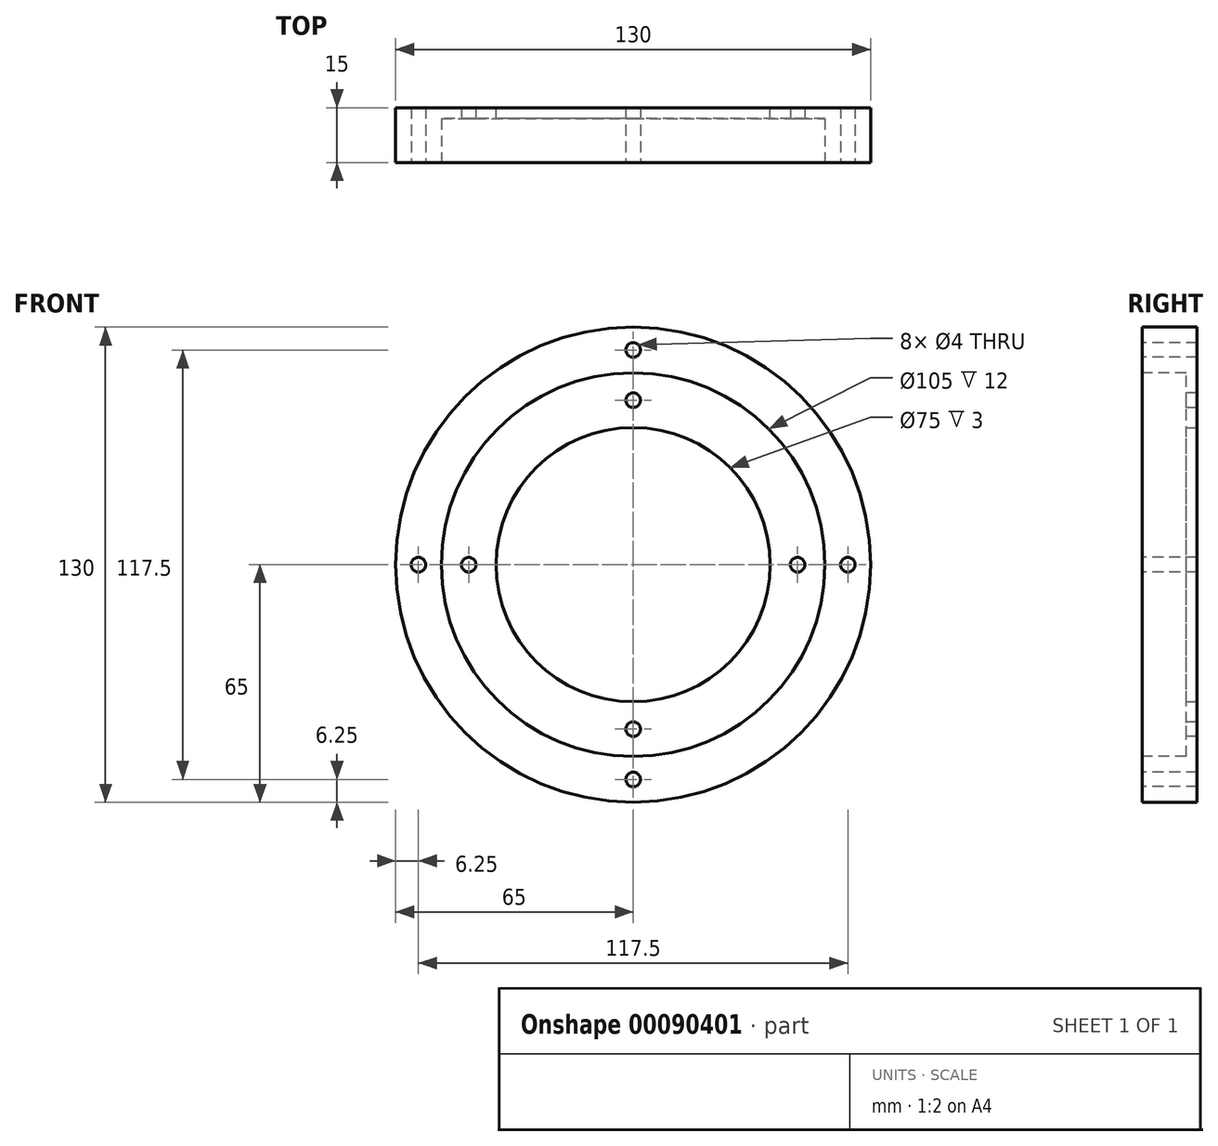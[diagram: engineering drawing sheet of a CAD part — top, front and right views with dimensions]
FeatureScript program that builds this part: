
annotation { "Feature Type Name" : "Feature", "Feature Type Description" : "" }
export const myFeature = defineFeature(function(context is Context, id is Id, definition is map)
    precondition{}
    {
        {
            var Q0;
            Q0=qCreatedBy(makeId("Front.planeOp"),FACE);
            var sketch = newSketch(context, id + "F0", { "sketchPlane" : qUnion([Q0])});
            skCircle(sketch, "E0", {"center": v(0, 0) * mm, "radius": 65 * mm});
            skSolve(sketch);
        }
        {
            var Q0;
            Q0 = qSketchRegion(id + "F0", true);
            extrude(context, id + "F1", {"entities" : qUnion([Q0]), "depth" : 15 * mm});
        }
        {
            var Q0;
            Q0=makeQuery(id+"F1.opExtrude","CAP_FACE",FACE,{"disambiguationData":[OSD([sQuery(id+"F0.wireOp",EDGE,"E0")])],"isStart":false});
            var sketch = newSketch(context, id + "F2", { "sketchPlane" : qUnion([Q0])});
            skCircle(sketch, "E1", {"center": v(0, 0) * mm, "radius": 52.5 * mm});
            skSolve(sketch);
        }
        {
            var Q0;
            Q0=makeQuery(id+"F2.imprint","IMPRINT",FACE,{"disambiguationData":[TD([[makeQuery(id+"F2.imprint","IMPRINT",EDGE,{"derivedFrom":sQuery(id+"F2.wireOp",EDGE,"E1")}),1.0]])]});
            extrude(context, id + "F3", {"entities" : qUnion([Q0]), "operationType" : NewBodyOperationType.REMOVE, "oppositeDirection" : true, "depth" : 12 * mm});
        }
        {
            var Q0;
            Q0=makeQuery(id+"F1.opExtrude","CAP_FACE",FACE,{"disambiguationData":[OSD([sQuery(id+"F0.wireOp",EDGE,"E0")])],"isStart":false});
            var sketch = newSketch(context, id + "F4", { "sketchPlane" : qUnion([Q0])});
            skCircle(sketch, "E2", {"center": v(0, 0) * mm, "radius": 58.75 * mm});
            skPoint(sketch, "E3", {"position": v(0, 58.75) * mm});
            skPoint(sketch, "E4", {"position": v(58.75, 0) * mm});
            skPoint(sketch, "E5", {"position": v(0, -58.75) * mm});
            skPoint(sketch, "E6", {"position": v(-58.75, 0) * mm});
            skSolve(sketch);
        }
        {
            var Q0;
            Q0=sQuery(id+"F4.wireOp",VERTEX,"E6");
            var Q1;
            Q1=sQuery(id+"F4.wireOp",VERTEX,"E3");
            var Q2;
            Q2=sQuery(id+"F4.wireOp",VERTEX,"E4");
            var Q3;
            Q3=sQuery(id+"F4.wireOp",VERTEX,"E5");
            var Q4;
            Q4=makeQuery(id+"F1.opExtrude","SWEPT_BODY",BODY,{"disambiguationData":[OSD([sQuery(id+"F0.wireOp",EDGE,"E0")])]});
            hole(context, id + "F5", {"style" : HoleStyle.SIMPLE, "endStyle" : HoleEndStyle.BLIND, "holeDiameter" : 4 * mm, "holeDepth" : 25 * mm, "startFromSketch" : true, "locations" : qUnion([Q0, Q1, Q2, Q3]), "scope" : qUnion([Q4])});
        }
        {
            var Q0;
            Q0=makeQuery(id+"F3.boolean.opBoolean","COPY",FACE,{"derivedFrom":makeQuery(id+"F3.opExtrude","CAP_FACE",FACE,{"disambiguationData":[OSD([sQuery(id+"F2.wireOp",EDGE,"E1")])],"isStart":false})});
            var sketch = newSketch(context, id + "F6", { "sketchPlane" : qUnion([Q0])});
            skCircle(sketch, "E7", {"center": v(0, 0) * mm, "radius": 45 * mm});
            skPoint(sketch, "E8", {"position": v(-45, 0) * mm});
            skPoint(sketch, "E9", {"position": v(0, -45) * mm});
            skPoint(sketch, "E10", {"position": v(0, 45) * mm});
            skPoint(sketch, "E11", {"position": v(45, 0) * mm});
            skSolve(sketch);
        }
        {
            var Q0;
            Q0=sQuery(id+"F6.wireOp",VERTEX,"E10");
            var Q1;
            Q1=sQuery(id+"F6.wireOp",VERTEX,"E8");
            var Q2;
            Q2=sQuery(id+"F6.wireOp",VERTEX,"E11");
            var Q3;
            Q3=sQuery(id+"F6.wireOp",VERTEX,"E9");
            var Q4;
            Q4=makeQuery(id+"F1.opExtrude","SWEPT_BODY",BODY,{"disambiguationData":[OSD([sQuery(id+"F0.wireOp",EDGE,"E0")])]});
            hole(context, id + "F7", {"style" : HoleStyle.SIMPLE, "endStyle" : HoleEndStyle.BLIND, "holeDiameter" : 4 * mm, "holeDepth" : 25 * mm, "startFromSketch" : true, "locations" : qUnion([Q0, Q1, Q2, Q3]), "scope" : qUnion([Q4])});
        }
        {
            var Q0;
            Q0=makeQuery(id+"F1.opExtrude","CAP_FACE",FACE,{"disambiguationData":[OSD([sQuery(id+"F0.wireOp",EDGE,"E0")])],"isStart":true});
            var sketch = newSketch(context, id + "F8", { "sketchPlane" : qUnion([Q0])});
            skCircle(sketch, "E12", {"center": v(0, 0) * mm, "radius": 37.5 * mm});
            skSolve(sketch);
        }
        {
            var Q0;
            Q0=makeQuery(id+"F8.imprint","IMPRINT",FACE,{"disambiguationData":[TD([[makeQuery(id+"F8.imprint","IMPRINT",EDGE,{"derivedFrom":sQuery(id+"F8.wireOp",EDGE,"E12")}),1.0]])]});
            extrude(context, id + "F9", {"entities" : qUnion([Q0]), "operationType" : NewBodyOperationType.REMOVE, "oppositeDirection" : true, "depth" : 25 * mm});
        }
    });
